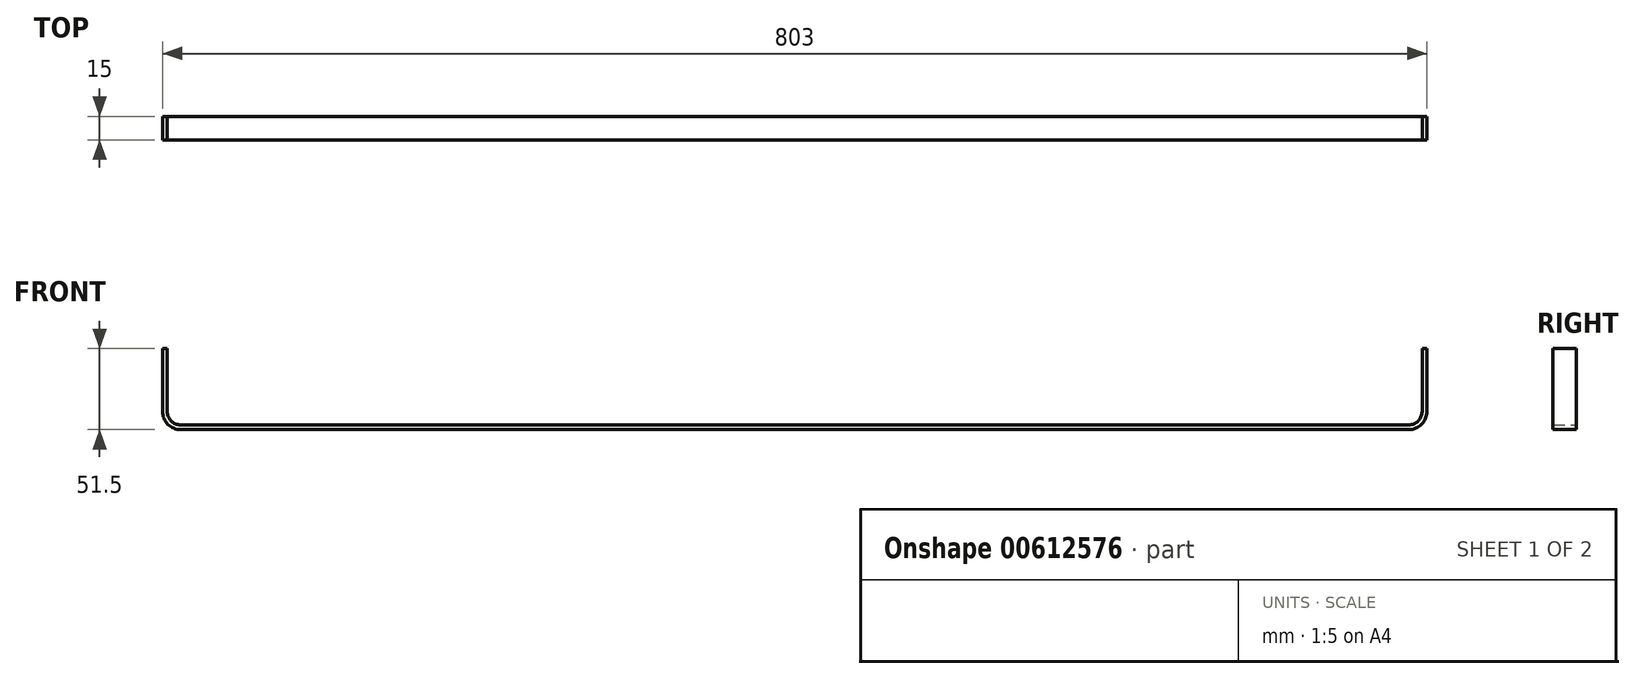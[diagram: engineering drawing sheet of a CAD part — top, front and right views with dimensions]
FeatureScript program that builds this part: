
annotation { "Feature Type Name" : "Feature", "Feature Type Description" : "" }
export const myFeature = defineFeature(function(context is Context, id is Id, definition is map)
    precondition{}
    {
        {
            var Q0;
            Q0=qCreatedBy(makeId("Front.planeOp"),FACE);
            var sketch = newSketch(context, id + "F0", { "sketchPlane" : qUnion([Q0])});
            skLineSegment(sketch, "E0", {"start": v(0, 0) * mm, "end": v(0, -40) * mm});
            skLineSegment(sketch, "E1", {"start": v(10, -50) * mm, "end": v(790, -50) * mm});
            skLineSegment(sketch, "E2", {"start": v(800, -40) * mm, "end": v(800, 0) * mm});
            skPoint(sketch, "E3.visualSharp", {"position": v(0, -50) * mm});
            skArc(sketch, "E3.filletArc", {"start": v(0, -40) * mm, "mid": v(2.93, -47.07) * mm, "end": v(10, -50) * mm});
            skPoint(sketch, "E4.visualSharp", {"position": v(800, -50) * mm});
            skArc(sketch, "E4.filletArc", {"start": v(790, -50) * mm, "mid": v(797.07, -47.07) * mm, "end": v(800, -40) * mm});
            skSolve(sketch);
        }
        {
            var Q0;
            Q0=qCreatedBy(makeId("Top.planeOp"),FACE);
            var sketch = newSketch(context, id + "F1", { "sketchPlane" : qUnion([Q0])});
            skLineSegment(sketch, "E5.bottom", {"start": v(1.5, -7.5) * mm, "end": v(-1.5, -7.5) * mm});
            skLineSegment(sketch, "E5.top", {"start": v(1.5, 7.5) * mm, "end": v(-1.5, 7.5) * mm});
            skLineSegment(sketch, "E5.left", {"start": v(1.5, -7.5) * mm, "end": v(1.5, 7.5) * mm});
            skLineSegment(sketch, "E5.right", {"start": v(-1.5, -7.5) * mm, "end": v(-1.5, 7.5) * mm});
            skPoint(sketch, "E5.middle", {"position": v(0, 0) * mm});
            skSolve(sketch);
        }
        {
            var Q0;
            Q0=makeQuery(id+"F1.imprint","IMPRINT",FACE,{"disambiguationData":[TD([[makeQuery(id+"F1.imprint","IMPRINT",EDGE,{"derivedFrom":sQuery(id+"F1.wireOp",EDGE,"E5.bottom")}),-1.0]])]});
            var Q1;
            Q1=sQuery(id+"F0.wireOp",EDGE,"E0");
            var Q2;
            Q2=sQuery(id+"F0.wireOp",EDGE,"E3.filletArc");
            var Q3;
            Q3=sQuery(id+"F0.wireOp",EDGE,"E1");
            var Q4;
            Q4=sQuery(id+"F0.wireOp",EDGE,"E4.filletArc");
            var Q5;
            Q5=sQuery(id+"F0.wireOp",EDGE,"E2");
            sweep(context, id + "F2", {"profiles" : qUnion([Q0]), "path" : qUnion([Q1, Q2, Q3, Q4, Q5])});
        }
    });
